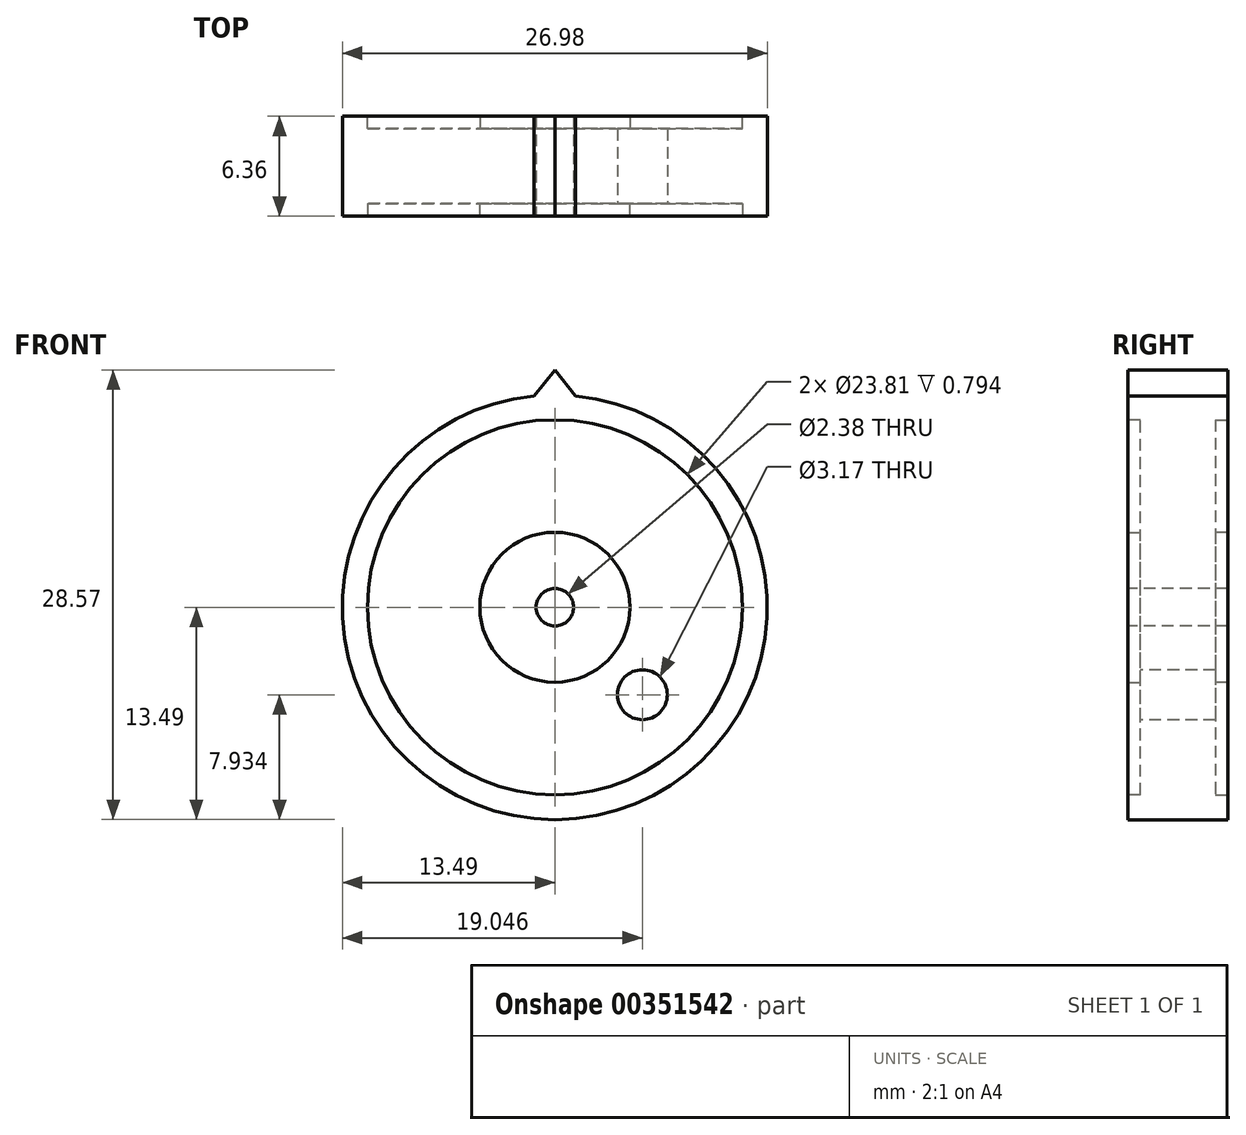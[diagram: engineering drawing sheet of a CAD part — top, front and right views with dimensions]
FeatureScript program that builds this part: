
annotation { "Feature Type Name" : "Feature", "Feature Type Description" : "" }
export const myFeature = defineFeature(function(context is Context, id is Id, definition is map)
    precondition{}
    {
        {
            var Q0;
            Q0=qCreatedBy(makeId("Front.planeOp"),FACE);
            var sketch = newSketch(context, id + "F0", { "sketchPlane" : qUnion([Q0])});
            skCircle(sketch, "E0", {"center": v(0, 0) * mm, "radius": 13.5 * mm});
            skSolve(sketch);
        }
        {
            var Q0;
            Q0 = qSketchRegion(id + "F0", true);
            extrude(context, id + "F1", {"entities" : qUnion([Q0]), "depth" : 6.35 * mm, "symmetric" : true});
        }
        {
            var Q0;
            Q0=makeQuery(id+"F1.opExtrude","CAP_FACE",FACE,{"disambiguationData":[OSD([sQuery(id+"F0.wireOp",EDGE,"E0")])],"isStart":false});
            var sketch = newSketch(context, id + "F2", { "sketchPlane" : qUnion([Q0])});
            skLineSegment(sketch, "E1", {"start": v(-1.32, 13.43) * mm, "end": v(0, 15.08) * mm});
            skLineSegment(sketch, "E2", {"start": v(0, 15.08) * mm, "end": v(1.3, 13.43) * mm});
            skArc(sketch, "E3.0", {"start": v(1.3, 13.43) * mm, "mid": v(0, 13.5) * mm, "end": v(-1.32, 13.43) * mm});
            skLineSegment(sketch, "E4", {"start": v(0, 15.08) * mm, "end": v(0, 13.5) * mm});
            skSolve(sketch);
        }
        {
            var Q0;
            Q0 = qSketchRegion(id + "F2", true);
            var Q1;
            Q1=makeQuery(id+"F1.opExtrude","CAP_FACE",FACE,{"disambiguationData":[OSD([sQuery(id+"F0.wireOp",EDGE,"E0")])],"isStart":true});
            extrude(context, id + "F3", {"entities" : qUnion([Q0]), "operationType" : NewBodyOperationType.ADD, "endBound" : BoundingType.UP_TO_SURFACE, "oppositeDirection" : true, "endBoundEntityFace" : qUnion([Q1]), "depth" : 25.4 * mm});
        }
        {
            var Q0;
            {var subQ0=sQuery(id+"F2.wireOp",EDGE,"E3.0");var subQ1=sQuery(id+"F2.wireOp",EDGE,"E2");var subQ2=sQuery(id+"F2.wireOp",EDGE,"E1");Q0=makeQuery(id+"Fv2Ua4LIVU1my1x_1.29.F3.boolean.opBoolean","MERGE",FACE,{"derivedFrom":[makeQuery(id+"Fv2Ua4LIVU1my1x_1.28.F3.boolean.opBoolean","MERGE",FACE,{"derivedFrom":[makeQuery(id+"Fv2Ua4LIVU1my1x_1.27.F3.boolean.opBoolean","MERGE",FACE,{"derivedFrom":[makeQuery(id+"Fv2Ua4LIVU1my1x_1.26.F3.boolean.opBoolean","MERGE",FACE,{"derivedFrom":[makeQuery(id+"Fv2Ua4LIVU1my1x_1.25.F3.boolean.opBoolean","MERGE",FACE,{"derivedFrom":[makeQuery(id+"Fv2Ua4LIVU1my1x_1.24.F3.boolean.opBoolean","MERGE",FACE,{"derivedFrom":[makeQuery(id+"Fv2Ua4LIVU1my1x_1.23.F3.boolean.opBoolean","MERGE",FACE,{"derivedFrom":[makeQuery(id+"Fv2Ua4LIVU1my1x_1.22.F3.boolean.opBoolean","MERGE",FACE,{"derivedFrom":[makeQuery(id+"Fv2Ua4LIVU1my1x_1.21.F3.boolean.opBoolean","MERGE",FACE,{"derivedFrom":[makeQuery(id+"Fv2Ua4LIVU1my1x_1.20.F3.boolean.opBoolean","MERGE",FACE,{"derivedFrom":[makeQuery(id+"Fv2Ua4LIVU1my1x_1.19.F3.boolean.opBoolean","MERGE",FACE,{"derivedFrom":[makeQuery(id+"Fv2Ua4LIVU1my1x_1.18.F3.boolean.opBoolean","MERGE",FACE,{"derivedFrom":[makeQuery(id+"Fv2Ua4LIVU1my1x_1.17.F3.boolean.opBoolean","MERGE",FACE,{"derivedFrom":[makeQuery(id+"Fv2Ua4LIVU1my1x_1.16.F3.boolean.opBoolean","MERGE",FACE,{"derivedFrom":[makeQuery(id+"Fv2Ua4LIVU1my1x_1.15.F3.boolean.opBoolean","MERGE",FACE,{"derivedFrom":[makeQuery(id+"Fv2Ua4LIVU1my1x_1.14.F3.boolean.opBoolean","MERGE",FACE,{"derivedFrom":[makeQuery(id+"Fv2Ua4LIVU1my1x_1.13.F3.boolean.opBoolean","MERGE",FACE,{"derivedFrom":[makeQuery(id+"Fv2Ua4LIVU1my1x_1.12.F3.boolean.opBoolean","MERGE",FACE,{"derivedFrom":[makeQuery(id+"Fv2Ua4LIVU1my1x_1.11.F3.boolean.opBoolean","MERGE",FACE,{"derivedFrom":[makeQuery(id+"Fv2Ua4LIVU1my1x_1.10.F3.boolean.opBoolean","MERGE",FACE,{"derivedFrom":[makeQuery(id+"Fv2Ua4LIVU1my1x_1.9.F3.boolean.opBoolean","MERGE",FACE,{"derivedFrom":[makeQuery(id+"Fv2Ua4LIVU1my1x_1.8.F3.boolean.opBoolean","MERGE",FACE,{"derivedFrom":[makeQuery(id+"Fv2Ua4LIVU1my1x_1.7.F3.boolean.opBoolean","MERGE",FACE,{"derivedFrom":[makeQuery(id+"Fv2Ua4LIVU1my1x_1.6.F3.boolean.opBoolean","MERGE",FACE,{"derivedFrom":[makeQuery(id+"Fv2Ua4LIVU1my1x_1.5.F3.boolean.opBoolean","MERGE",FACE,{"derivedFrom":[makeQuery(id+"Fv2Ua4LIVU1my1x_1.4.F3.boolean.opBoolean","MERGE",FACE,{"derivedFrom":[makeQuery(id+"Fv2Ua4LIVU1my1x_1.3.F3.boolean.opBoolean","MERGE",FACE,{"derivedFrom":[makeQuery(id+"Fv2Ua4LIVU1my1x_1.2.F3.boolean.opBoolean","MERGE",FACE,{"derivedFrom":[makeQuery(id+"Fv2Ua4LIVU1my1x_1.1.F3.boolean.opBoolean","MERGE",FACE,{"derivedFrom":[makeQuery(id+"F3.boolean.opBoolean","MERGE",FACE,{"derivedFrom":[makeQuery(id+"F1.opExtrude","CAP_FACE",FACE,{"disambiguationData":[OSD([sQuery(id+"F0.wireOp",EDGE,"E0")])],"isStart":false}),makeQuery(id+"F3.opExtrude","CAP_FACE",FACE,{"disambiguationData":[OSD([subQ2,subQ1,subQ0])],"isStart":true})]}),makeQuery(id+"Fv2Ua4LIVU1my1x_1.1.F3.opExtrude","CAP_FACE",FACE,{"disambiguationData":[OSD([subQ2,subQ1,subQ0])],"isStart":true})]}),makeQuery(id+"Fv2Ua4LIVU1my1x_1.2.F3.opExtrude","CAP_FACE",FACE,{"disambiguationData":[OSD([subQ2,subQ1,subQ0])],"isStart":true})]}),makeQuery(id+"Fv2Ua4LIVU1my1x_1.3.F3.opExtrude","CAP_FACE",FACE,{"disambiguationData":[OSD([subQ2,subQ1,subQ0])],"isStart":true})]}),makeQuery(id+"Fv2Ua4LIVU1my1x_1.4.F3.opExtrude","CAP_FACE",FACE,{"disambiguationData":[OSD([subQ2,subQ1,subQ0])],"isStart":true})]}),makeQuery(id+"Fv2Ua4LIVU1my1x_1.5.F3.opExtrude","CAP_FACE",FACE,{"disambiguationData":[OSD([subQ2,subQ1,subQ0])],"isStart":true})]}),makeQuery(id+"Fv2Ua4LIVU1my1x_1.6.F3.opExtrude","CAP_FACE",FACE,{"disambiguationData":[OSD([subQ2,subQ1,subQ0])],"isStart":true})]}),makeQuery(id+"Fv2Ua4LIVU1my1x_1.7.F3.opExtrude","CAP_FACE",FACE,{"disambiguationData":[OSD([subQ2,subQ1,subQ0])],"isStart":true})]}),makeQuery(id+"Fv2Ua4LIVU1my1x_1.8.F3.opExtrude","CAP_FACE",FACE,{"disambiguationData":[OSD([subQ2,subQ1,subQ0])],"isStart":true})]}),makeQuery(id+"Fv2Ua4LIVU1my1x_1.9.F3.opExtrude","CAP_FACE",FACE,{"disambiguationData":[OSD([subQ2,subQ1,subQ0])],"isStart":true})]}),makeQuery(id+"Fv2Ua4LIVU1my1x_1.10.F3.opExtrude","CAP_FACE",FACE,{"disambiguationData":[OSD([subQ2,subQ1,subQ0])],"isStart":true})]}),makeQuery(id+"Fv2Ua4LIVU1my1x_1.11.F3.opExtrude","CAP_FACE",FACE,{"disambiguationData":[OSD([subQ2,subQ1,subQ0])],"isStart":true})]}),makeQuery(id+"Fv2Ua4LIVU1my1x_1.12.F3.opExtrude","CAP_FACE",FACE,{"disambiguationData":[OSD([subQ2,subQ1,subQ0])],"isStart":true})]}),makeQuery(id+"Fv2Ua4LIVU1my1x_1.13.F3.opExtrude","CAP_FACE",FACE,{"disambiguationData":[OSD([subQ2,subQ1,subQ0])],"isStart":true})]}),makeQuery(id+"Fv2Ua4LIVU1my1x_1.14.F3.opExtrude","CAP_FACE",FACE,{"disambiguationData":[OSD([subQ2,subQ1,subQ0])],"isStart":true})]}),makeQuery(id+"Fv2Ua4LIVU1my1x_1.15.F3.opExtrude","CAP_FACE",FACE,{"disambiguationData":[OSD([subQ2,subQ1,subQ0])],"isStart":true})]}),makeQuery(id+"Fv2Ua4LIVU1my1x_1.16.F3.opExtrude","CAP_FACE",FACE,{"disambiguationData":[OSD([subQ2,subQ1,subQ0])],"isStart":true})]}),makeQuery(id+"Fv2Ua4LIVU1my1x_1.17.F3.opExtrude","CAP_FACE",FACE,{"disambiguationData":[OSD([subQ2,subQ1,subQ0])],"isStart":true})]}),makeQuery(id+"Fv2Ua4LIVU1my1x_1.18.F3.opExtrude","CAP_FACE",FACE,{"disambiguationData":[OSD([subQ2,subQ1,subQ0])],"isStart":true})]}),makeQuery(id+"Fv2Ua4LIVU1my1x_1.19.F3.opExtrude","CAP_FACE",FACE,{"disambiguationData":[OSD([subQ2,subQ1,subQ0])],"isStart":true})]}),makeQuery(id+"Fv2Ua4LIVU1my1x_1.20.F3.opExtrude","CAP_FACE",FACE,{"disambiguationData":[OSD([subQ2,subQ1,subQ0])],"isStart":true})]}),makeQuery(id+"Fv2Ua4LIVU1my1x_1.21.F3.opExtrude","CAP_FACE",FACE,{"disambiguationData":[OSD([subQ2,subQ1,subQ0])],"isStart":true})]}),makeQuery(id+"Fv2Ua4LIVU1my1x_1.22.F3.opExtrude","CAP_FACE",FACE,{"disambiguationData":[OSD([subQ2,subQ1,subQ0])],"isStart":true})]}),makeQuery(id+"Fv2Ua4LIVU1my1x_1.23.F3.opExtrude","CAP_FACE",FACE,{"disambiguationData":[OSD([subQ2,subQ1,subQ0])],"isStart":true})]}),makeQuery(id+"Fv2Ua4LIVU1my1x_1.24.F3.opExtrude","CAP_FACE",FACE,{"disambiguationData":[OSD([subQ2,subQ1,subQ0])],"isStart":true})]}),makeQuery(id+"Fv2Ua4LIVU1my1x_1.25.F3.opExtrude","CAP_FACE",FACE,{"disambiguationData":[OSD([subQ2,subQ1,subQ0])],"isStart":true})]}),makeQuery(id+"Fv2Ua4LIVU1my1x_1.26.F3.opExtrude","CAP_FACE",FACE,{"disambiguationData":[OSD([subQ2,subQ1,subQ0])],"isStart":true})]}),makeQuery(id+"Fv2Ua4LIVU1my1x_1.27.F3.opExtrude","CAP_FACE",FACE,{"disambiguationData":[OSD([subQ2,subQ1,subQ0])],"isStart":true})]}),makeQuery(id+"Fv2Ua4LIVU1my1x_1.28.F3.opExtrude","CAP_FACE",FACE,{"disambiguationData":[OSD([subQ2,subQ1,subQ0])],"isStart":true})]}),makeQuery(id+"Fv2Ua4LIVU1my1x_1.29.F3.opExtrude","CAP_FACE",FACE,{"disambiguationData":[OSD([subQ2,subQ1,subQ0])],"isStart":true})]});}
            var sketch = newSketch(context, id + "F4", { "sketchPlane" : qUnion([Q0])});
            skCircle(sketch, "E5", {"center": v(0, 0) * mm, "radius": 11.9 * mm});
            skSolve(sketch);
        }
        {
            var Q0;
            Q0 = qSketchRegion(id + "F4", true);
            extrude(context, id + "F5", {"entities" : qUnion([Q0]), "operationType" : NewBodyOperationType.REMOVE, "oppositeDirection" : true, "depth" : 0.8 * mm});
        }
        {
            var Q0;
            {var subQ0=sQuery(id+"F0.wireOp",EDGE,"E0");Q0=makeQuery(id+"Fv2Ua4LIVU1my1x_1.29.F3.boolean.opBoolean","MERGE",FACE,{"derivedFrom":[makeQuery(id+"Fv2Ua4LIVU1my1x_1.28.F3.boolean.opBoolean","MERGE",FACE,{"derivedFrom":[makeQuery(id+"Fv2Ua4LIVU1my1x_1.27.F3.boolean.opBoolean","MERGE",FACE,{"derivedFrom":[makeQuery(id+"Fv2Ua4LIVU1my1x_1.26.F3.boolean.opBoolean","MERGE",FACE,{"derivedFrom":[makeQuery(id+"Fv2Ua4LIVU1my1x_1.25.F3.boolean.opBoolean","MERGE",FACE,{"derivedFrom":[makeQuery(id+"Fv2Ua4LIVU1my1x_1.24.F3.boolean.opBoolean","MERGE",FACE,{"derivedFrom":[makeQuery(id+"Fv2Ua4LIVU1my1x_1.23.F3.boolean.opBoolean","MERGE",FACE,{"derivedFrom":[makeQuery(id+"Fv2Ua4LIVU1my1x_1.22.F3.boolean.opBoolean","MERGE",FACE,{"derivedFrom":[makeQuery(id+"Fv2Ua4LIVU1my1x_1.21.F3.boolean.opBoolean","MERGE",FACE,{"derivedFrom":[makeQuery(id+"Fv2Ua4LIVU1my1x_1.20.F3.boolean.opBoolean","MERGE",FACE,{"derivedFrom":[makeQuery(id+"Fv2Ua4LIVU1my1x_1.19.F3.boolean.opBoolean","MERGE",FACE,{"derivedFrom":[makeQuery(id+"Fv2Ua4LIVU1my1x_1.18.F3.boolean.opBoolean","MERGE",FACE,{"derivedFrom":[makeQuery(id+"Fv2Ua4LIVU1my1x_1.17.F3.boolean.opBoolean","MERGE",FACE,{"derivedFrom":[makeQuery(id+"Fv2Ua4LIVU1my1x_1.16.F3.boolean.opBoolean","MERGE",FACE,{"derivedFrom":[makeQuery(id+"Fv2Ua4LIVU1my1x_1.15.F3.boolean.opBoolean","MERGE",FACE,{"derivedFrom":[makeQuery(id+"Fv2Ua4LIVU1my1x_1.14.F3.boolean.opBoolean","MERGE",FACE,{"derivedFrom":[makeQuery(id+"Fv2Ua4LIVU1my1x_1.13.F3.boolean.opBoolean","MERGE",FACE,{"derivedFrom":[makeQuery(id+"Fv2Ua4LIVU1my1x_1.12.F3.boolean.opBoolean","MERGE",FACE,{"derivedFrom":[makeQuery(id+"Fv2Ua4LIVU1my1x_1.11.F3.boolean.opBoolean","MERGE",FACE,{"derivedFrom":[makeQuery(id+"Fv2Ua4LIVU1my1x_1.10.F3.boolean.opBoolean","MERGE",FACE,{"derivedFrom":[makeQuery(id+"Fv2Ua4LIVU1my1x_1.9.F3.boolean.opBoolean","MERGE",FACE,{"derivedFrom":[makeQuery(id+"Fv2Ua4LIVU1my1x_1.8.F3.boolean.opBoolean","MERGE",FACE,{"derivedFrom":[makeQuery(id+"Fv2Ua4LIVU1my1x_1.7.F3.boolean.opBoolean","MERGE",FACE,{"derivedFrom":[makeQuery(id+"Fv2Ua4LIVU1my1x_1.6.F3.boolean.opBoolean","MERGE",FACE,{"derivedFrom":[makeQuery(id+"Fv2Ua4LIVU1my1x_1.5.F3.boolean.opBoolean","MERGE",FACE,{"derivedFrom":[makeQuery(id+"Fv2Ua4LIVU1my1x_1.4.F3.boolean.opBoolean","MERGE",FACE,{"derivedFrom":[makeQuery(id+"Fv2Ua4LIVU1my1x_1.3.F3.boolean.opBoolean","MERGE",FACE,{"derivedFrom":[makeQuery(id+"Fv2Ua4LIVU1my1x_1.2.F3.boolean.opBoolean","MERGE",FACE,{"derivedFrom":[makeQuery(id+"Fv2Ua4LIVU1my1x_1.1.F3.boolean.opBoolean","MERGE",FACE,{"derivedFrom":[makeQuery(id+"F3.boolean.opBoolean","MERGE",FACE,{"derivedFrom":[makeQuery(id+"F1.opExtrude","CAP_FACE",FACE,{"disambiguationData":[OSD([subQ0])],"isStart":true}),makeQuery(id+"F3.opExtrude","CAP_FACE",FACE,{"disambiguationData":[OSD([subQ0])],"isStart":false})]}),makeQuery(id+"Fv2Ua4LIVU1my1x_1.1.F3.opExtrude","CAP_FACE",FACE,{"disambiguationData":[OSD([subQ0])],"isStart":false})]}),makeQuery(id+"Fv2Ua4LIVU1my1x_1.2.F3.opExtrude","CAP_FACE",FACE,{"disambiguationData":[OSD([subQ0])],"isStart":false})]}),makeQuery(id+"Fv2Ua4LIVU1my1x_1.3.F3.opExtrude","CAP_FACE",FACE,{"disambiguationData":[OSD([subQ0])],"isStart":false})]}),makeQuery(id+"Fv2Ua4LIVU1my1x_1.4.F3.opExtrude","CAP_FACE",FACE,{"disambiguationData":[OSD([subQ0])],"isStart":false})]}),makeQuery(id+"Fv2Ua4LIVU1my1x_1.5.F3.opExtrude","CAP_FACE",FACE,{"disambiguationData":[OSD([subQ0])],"isStart":false})]}),makeQuery(id+"Fv2Ua4LIVU1my1x_1.6.F3.opExtrude","CAP_FACE",FACE,{"disambiguationData":[OSD([subQ0])],"isStart":false})]}),makeQuery(id+"Fv2Ua4LIVU1my1x_1.7.F3.opExtrude","CAP_FACE",FACE,{"disambiguationData":[OSD([subQ0])],"isStart":false})]}),makeQuery(id+"Fv2Ua4LIVU1my1x_1.8.F3.opExtrude","CAP_FACE",FACE,{"disambiguationData":[OSD([subQ0])],"isStart":false})]}),makeQuery(id+"Fv2Ua4LIVU1my1x_1.9.F3.opExtrude","CAP_FACE",FACE,{"disambiguationData":[OSD([subQ0])],"isStart":false})]}),makeQuery(id+"Fv2Ua4LIVU1my1x_1.10.F3.opExtrude","CAP_FACE",FACE,{"disambiguationData":[OSD([subQ0])],"isStart":false})]}),makeQuery(id+"Fv2Ua4LIVU1my1x_1.11.F3.opExtrude","CAP_FACE",FACE,{"disambiguationData":[OSD([subQ0])],"isStart":false})]}),makeQuery(id+"Fv2Ua4LIVU1my1x_1.12.F3.opExtrude","CAP_FACE",FACE,{"disambiguationData":[OSD([subQ0])],"isStart":false})]}),makeQuery(id+"Fv2Ua4LIVU1my1x_1.13.F3.opExtrude","CAP_FACE",FACE,{"disambiguationData":[OSD([subQ0])],"isStart":false})]}),makeQuery(id+"Fv2Ua4LIVU1my1x_1.14.F3.opExtrude","CAP_FACE",FACE,{"disambiguationData":[OSD([subQ0])],"isStart":false})]}),makeQuery(id+"Fv2Ua4LIVU1my1x_1.15.F3.opExtrude","CAP_FACE",FACE,{"disambiguationData":[OSD([subQ0])],"isStart":false})]}),makeQuery(id+"Fv2Ua4LIVU1my1x_1.16.F3.opExtrude","CAP_FACE",FACE,{"disambiguationData":[OSD([subQ0])],"isStart":false})]}),makeQuery(id+"Fv2Ua4LIVU1my1x_1.17.F3.opExtrude","CAP_FACE",FACE,{"disambiguationData":[OSD([subQ0])],"isStart":false})]}),makeQuery(id+"Fv2Ua4LIVU1my1x_1.18.F3.opExtrude","CAP_FACE",FACE,{"disambiguationData":[OSD([subQ0])],"isStart":false})]}),makeQuery(id+"Fv2Ua4LIVU1my1x_1.19.F3.opExtrude","CAP_FACE",FACE,{"disambiguationData":[OSD([subQ0])],"isStart":false})]}),makeQuery(id+"Fv2Ua4LIVU1my1x_1.20.F3.opExtrude","CAP_FACE",FACE,{"disambiguationData":[OSD([subQ0])],"isStart":false})]}),makeQuery(id+"Fv2Ua4LIVU1my1x_1.21.F3.opExtrude","CAP_FACE",FACE,{"disambiguationData":[OSD([subQ0])],"isStart":false})]}),makeQuery(id+"Fv2Ua4LIVU1my1x_1.22.F3.opExtrude","CAP_FACE",FACE,{"disambiguationData":[OSD([subQ0])],"isStart":false})]}),makeQuery(id+"Fv2Ua4LIVU1my1x_1.23.F3.opExtrude","CAP_FACE",FACE,{"disambiguationData":[OSD([subQ0])],"isStart":false})]}),makeQuery(id+"Fv2Ua4LIVU1my1x_1.24.F3.opExtrude","CAP_FACE",FACE,{"disambiguationData":[OSD([subQ0])],"isStart":false})]}),makeQuery(id+"Fv2Ua4LIVU1my1x_1.25.F3.opExtrude","CAP_FACE",FACE,{"disambiguationData":[OSD([subQ0])],"isStart":false})]}),makeQuery(id+"Fv2Ua4LIVU1my1x_1.26.F3.opExtrude","CAP_FACE",FACE,{"disambiguationData":[OSD([subQ0])],"isStart":false})]}),makeQuery(id+"Fv2Ua4LIVU1my1x_1.27.F3.opExtrude","CAP_FACE",FACE,{"disambiguationData":[OSD([subQ0])],"isStart":false})]}),makeQuery(id+"Fv2Ua4LIVU1my1x_1.28.F3.opExtrude","CAP_FACE",FACE,{"disambiguationData":[OSD([subQ0])],"isStart":false})]}),makeQuery(id+"Fv2Ua4LIVU1my1x_1.29.F3.opExtrude","CAP_FACE",FACE,{"disambiguationData":[OSD([subQ0])],"isStart":false})]});}
            var sketch = newSketch(context, id + "F6", { "sketchPlane" : qUnion([Q0])});
            skCircle(sketch, "E6", {"center": v(0, 0) * mm, "radius": 11.9 * mm});
            skSolve(sketch);
        }
        {
            var Q0;
            Q0 = qSketchRegion(id + "F6", true);
            extrude(context, id + "F7", {"entities" : qUnion([Q0]), "operationType" : NewBodyOperationType.REMOVE, "oppositeDirection" : true, "depth" : 0.8 * mm});
        }
        {
            var Q0;
            Q0=makeQuery(id+"F5.boolean.opBoolean","COPY",FACE,{"derivedFrom":makeQuery(id+"F5.opExtrude","CAP_FACE",FACE,{"disambiguationData":[OSD([sQuery(id+"F4.wireOp",EDGE,"E5")])],"isStart":false})});
            var sketch = newSketch(context, id + "F8", { "sketchPlane" : qUnion([Q0])});
            skCircle(sketch, "E7", {"center": v(0, 0) * mm, "radius": 4.76 * mm});
            skSolve(sketch);
        }
        {
            var Q0;
            Q0=makeQuery(id+"F7.boolean.opBoolean","COPY",FACE,{"derivedFrom":makeQuery(id+"F7.opExtrude","CAP_FACE",FACE,{"disambiguationData":[OSD([sQuery(id+"F6.wireOp",EDGE,"E6")])],"isStart":false})});
            var sketch = newSketch(context, id + "F9", { "sketchPlane" : qUnion([Q0])});
            skCircle(sketch, "E8", {"center": v(0, 0) * mm, "radius": 4.76 * mm});
            skSolve(sketch);
        }
        {
            var Q0;
            Q0 = qSketchRegion(id + "F9", true);
            extrude(context, id + "F10", {"entities" : qUnion([Q0]), "operationType" : NewBodyOperationType.ADD, "depth" : 0.8 * mm});
        }
        {
            var Q0;
            Q0 = qSketchRegion(id + "F8", true);
            extrude(context, id + "F11", {"entities" : qUnion([Q0]), "operationType" : NewBodyOperationType.ADD, "depth" : 0.8 * mm});
        }
        {
            var Q0;
            Q0=makeQuery(id+"F11.opExtrude","CAP_FACE",FACE,{"disambiguationData":[OSD([sQuery(id+"F8.wireOp",EDGE,"E7")])],"isStart":false});
            var sketch = newSketch(context, id + "F12", { "sketchPlane" : qUnion([Q0])});
            skCircle(sketch, "E9", {"center": v(0, 0) * mm, "radius": 1.2 * mm});
            skSolve(sketch);
        }
        {
            var Q0;
            Q0 = qSketchRegion(id + "F12", true);
            extrude(context, id + "F13", {"entities" : qUnion([Q0]), "operationType" : NewBodyOperationType.REMOVE, "endBound" : BoundingType.THROUGH_ALL, "oppositeDirection" : true, "depth" : 25.4 * mm});
        }
        {
            var Q0;
            Q0=makeQuery(id+"F5.boolean.opBoolean","COPY",FACE,{"derivedFrom":makeQuery(id+"F5.opExtrude","CAP_FACE",FACE,{"disambiguationData":[OSD([sQuery(id+"F4.wireOp",EDGE,"E5")])],"isStart":false})});
            var sketch = newSketch(context, id + "F14", { "sketchPlane" : qUnion([Q0])});
            skCircle(sketch, "E10", {"center": v(5.56, -5.56) * mm, "radius": 1.59 * mm});
            skSolve(sketch);
        }
        {
            var Q0;
            Q0 = qSketchRegion(id + "F14", true);
            extrude(context, id + "F15", {"entities" : qUnion([Q0]), "operationType" : NewBodyOperationType.REMOVE, "endBound" : BoundingType.THROUGH_ALL, "oppositeDirection" : true, "depth" : 25.4 * mm});
        }
    });
